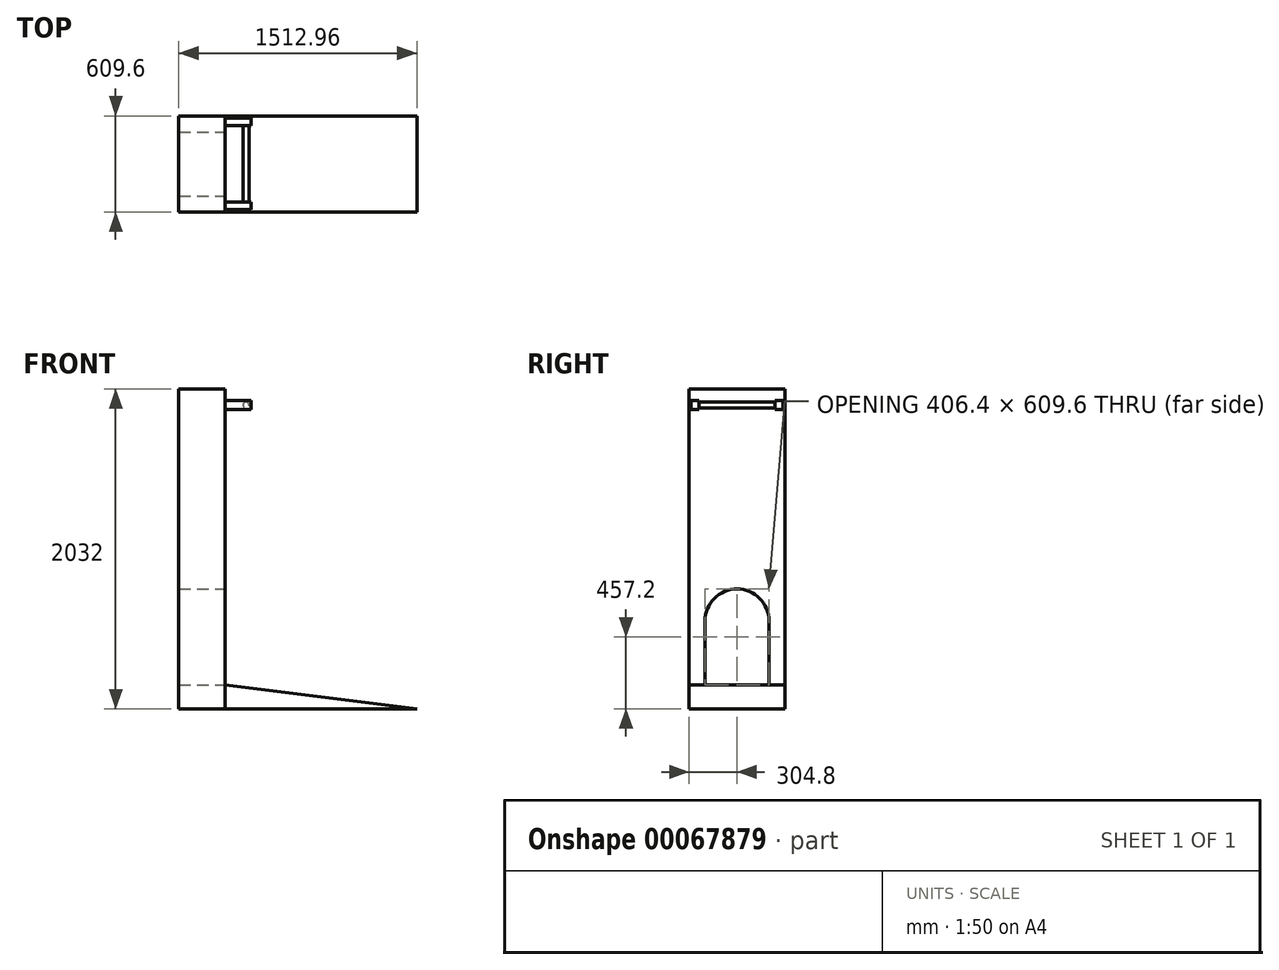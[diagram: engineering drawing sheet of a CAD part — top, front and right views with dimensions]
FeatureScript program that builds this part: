
annotation { "Feature Type Name" : "Feature", "Feature Type Description" : "" }
export const myFeature = defineFeature(function(context is Context, id is Id, definition is map)
    precondition{}
    {
        {
            var Q0;
            Q0=qCreatedBy(makeId("Front.planeOp"),FACE);
            var sketch = newSketch(context, id + "F0", { "sketchPlane" : qUnion([Q0])});
            skLineSegment(sketch, "E0", {"start": v(0, 0) * mm, "end": v(-1219.2, 0) * mm});
            skLineSegment(sketch, "E1", {"start": v(-1219.2, 0) * mm, "end": v(-1219.2, 152.4) * mm});
            skLineSegment(sketch, "E2", {"start": v(-1219.2, 152.4) * mm, "end": v(0, 0) * mm});
            skSolve(sketch);
        }
        {
            var Q0;
            Q0=makeQuery(id+"F0.imprint","IMPRINT",FACE,{"disambiguationData":[TD([[makeQuery(id+"F0.imprint","IMPRINT",EDGE,{"derivedFrom":sQuery(id+"F0.wireOp",EDGE,"E0")}),-1.0]])]});
            extrude(context, id + "F1", {"entities" : qUnion([Q0]), "depth" : 609.6 * mm});
        }
        {
            var Q0;
            Q0=makeQuery(id+"F1.opExtrude","SWEPT_FACE",FACE,{"disambiguationData":[OSD([sQuery(id+"F0.wireOp",EDGE,"E0")])]});
            var sketch = newSketch(context, id + "F2", { "sketchPlane" : qUnion([Q0])});
            skLineSegment(sketch, "E3.bottom", {"start": v(-1219.2, 609.6) * mm, "end": v(-1512.96, 609.6) * mm});
            skLineSegment(sketch, "E3.top", {"start": v(-1219.2, 0) * mm, "end": v(-1512.96, 0) * mm});
            skLineSegment(sketch, "E3.left", {"start": v(-1219.2, 609.6) * mm, "end": v(-1219.2, 0) * mm});
            skLineSegment(sketch, "E3.right", {"start": v(-1512.96, 609.6) * mm, "end": v(-1512.96, 0) * mm});
            skSolve(sketch);
        }
        {
            var Q0;
            Q0=qSketchRegion(id+"F2",true);
            extrude(context, id + "F3", {"entities" : qUnion([Q0]), "oppositeDirection" : true, "depth" : 2032 * mm});
        }
        {
            var Q0;
            Q0=makeQuery(id+"F3.opExtrude","SWEPT_FACE",FACE,{"disambiguationData":[OSD([sQuery(id+"F2.wireOp",EDGE,"E3.left")])]});
            var sketch = newSketch(context, id + "F4", { "sketchPlane" : qUnion([Q0])});
            skLineSegment(sketch, "E4.bottom", {"start": v(-596.08, 1902.3) * mm, "end": v(-546.92, 1902.3) * mm});
            skLineSegment(sketch, "E4.top", {"start": v(-596.08, 1958.5) * mm, "end": v(-546.92, 1958.5) * mm});
            skLineSegment(sketch, "E4.left", {"start": v(-596.08, 1958.5) * mm, "end": v(-596.08, 1902.3) * mm});
            skLineSegment(sketch, "E4.right", {"start": v(-546.92, 1958.5) * mm, "end": v(-546.92, 1902.3) * mm});
            skLineSegment(sketch, "E5", {"start": v(-304.8, 2032) * mm, "end": v(-304.8, 1268.99) * mm, "construction": true});
            skLineSegment(sketch, "E6.MirrorCS", {"start": v(-13.52, 1902.3) * mm, "end": v(-62.68, 1902.3) * mm});
            skLineSegment(sketch, "E7.MirrorCS", {"start": v(-13.52, 1958.5) * mm, "end": v(-62.68, 1958.5) * mm});
            skLineSegment(sketch, "E8.MirrorCS", {"start": v(-62.68, 1958.5) * mm, "end": v(-62.68, 1902.3) * mm});
            skLineSegment(sketch, "E9.MirrorCS", {"start": v(-13.52, 1958.5) * mm, "end": v(-13.52, 1902.3) * mm});
            skPoint(sketch, "E10", {"position": v(-571.5, 1902.3) * mm});
            skPoint(sketch, "E11", {"position": v(-38.1, 1902.3) * mm});
            skPoint(sketch, "E12", {"position": v(-62.68, 1930.4) * mm});
            skSolve(sketch);
        }
        {
            var Q0;
            Q0=qSketchRegion(id+"F4",true);
            extrude(context, id + "F5", {"entities" : qUnion([Q0]), "operationType" : NewBodyOperationType.ADD, "depth" : 165.1 * mm});
        }
        {
            var Q0;
            Q0=makeQuery(id+"F5.opExtrude","SWEPT_FACE",FACE,{"disambiguationData":[OSD([sQuery(id+"F4.wireOp",EDGE,"E4.right")])]});
            var sketch = newSketch(context, id + "F6", { "sketchPlane" : qUnion([Q0])});
            skLineSegment(sketch, "E13", {"start": v(1054.1, 1930.4) * mm, "end": v(1219.2, 1930.4) * mm, "construction": true});
            skCircle(sketch, "E14", {"center": v(1085.85, 1930.4) * mm, "radius": 19.05 * mm});
            skSolve(sketch);
        }
        {
            var Q0;
            Q0=makeQuery(id+"F6.imprint","IMPRINT",FACE,{"disambiguationData":[TD([[makeQuery(id+"F6.imprint","IMPRINT",EDGE,{"derivedFrom":sQuery(id+"F6.wireOp",EDGE,"E14")}),1.0]])]});
            extrude(context, id + "F7", {"entities" : qUnion([Q0]), "operationType" : NewBodyOperationType.ADD, "endBound" : BoundingType.UP_TO_NEXT, "depth" : 25.4 * mm});
        }
        {
            var Q0;
            Q0=makeQuery(id+"F3.opExtrude","SWEPT_FACE",FACE,{"disambiguationData":[OSD([sQuery(id+"F2.wireOp",EDGE,"E3.left")])]});
            var sketch = newSketch(context, id + "F8", { "sketchPlane" : qUnion([Q0])});
            skLineSegment(sketch, "E15", {"start": v(-508, 152.4) * mm, "end": v(-508, 558.8) * mm});
            skLineSegment(sketch, "E16", {"start": v(-101.6, 152.4) * mm, "end": v(-101.6, 558.8) * mm});
            skArc(sketch, "E17", {"start": v(-508, 558.8) * mm, "mid": v(-304.8, 762) * mm, "end": v(-101.6, 558.8) * mm});
            skPoint(sketch, "E18", {"position": v(-304.8, 762) * mm});
            skLineSegment(sketch, "E19", {"start": v(-304.8, 558.8) * mm, "end": v(-304.8, 152.4) * mm, "construction": true});
            skLineSegment(sketch, "E20", {"start": v(-508, 152.4) * mm, "end": v(-101.6, 152.4) * mm});
            skSolve(sketch);
        }
        {
            var Q0;
            Q0=makeQuery(id+"F8.imprint","IMPRINT",FACE,{"disambiguationData":[TD([[makeQuery(id+"F8.imprint","IMPRINT",EDGE,{"derivedFrom":sQuery(id+"F8.wireOp",EDGE,"E15")}),-1.0]])]});
            extrude(context, id + "F9", {"entities" : qUnion([Q0]), "operationType" : NewBodyOperationType.REMOVE, "endBound" : BoundingType.UP_TO_NEXT, "oppositeDirection" : true, "depth" : 25.4 * mm});
        }
    });
